# Revit family: LEGRAND_NON INTERLOCKED SOCKETS_SURFACE MOUNTED_IP66_230_SYMBOL
name_source: partatom
category: Annotations génériques
revit_build: Autodesk Revit 2018 (Build: 20170223_1515(x64)
units: mm (PartAtom-declared; Revit-internal decimal feet)

## family parameters
Conserve la lisibilité du texte = Non
Partagée = Non
Rotation avec le composant = Non

## types (9) — shared parameters
3P+H+N = Non
diameter symbol = 10 mm  [stored 0.0328084 ft]
interlocked sockets = Non
lock radius = 0.8 mm  [stored 0.00262467 ft]
pole radius = 1 mm  [stored 0.00328084 ft]
radius symbol = 5 mm  [stored 0.0164042 ft]

## per-type parameters (varying)
| type | 2P+H | 3P+H |
| Symbol ref.051126 | Oui | Non |
| Symbol ref.051127 | Non | Oui |
| Symbol ref.051146 | Oui | Non |
| Symbol ref.053046 | Oui | Non |
| Symbol ref.053911 | Oui | Non |
| Symbol ref.059326 | Oui | Non |
| Symbol ref.051147 | Non | Oui |
| Symbol ref.053047 | Non | Oui |
| Symbol ref.059327 | Non | Oui |

note: [stored X ft] marks values corroborated as IEEE doubles in the binary element streams (Revit-internal decimal feet)
